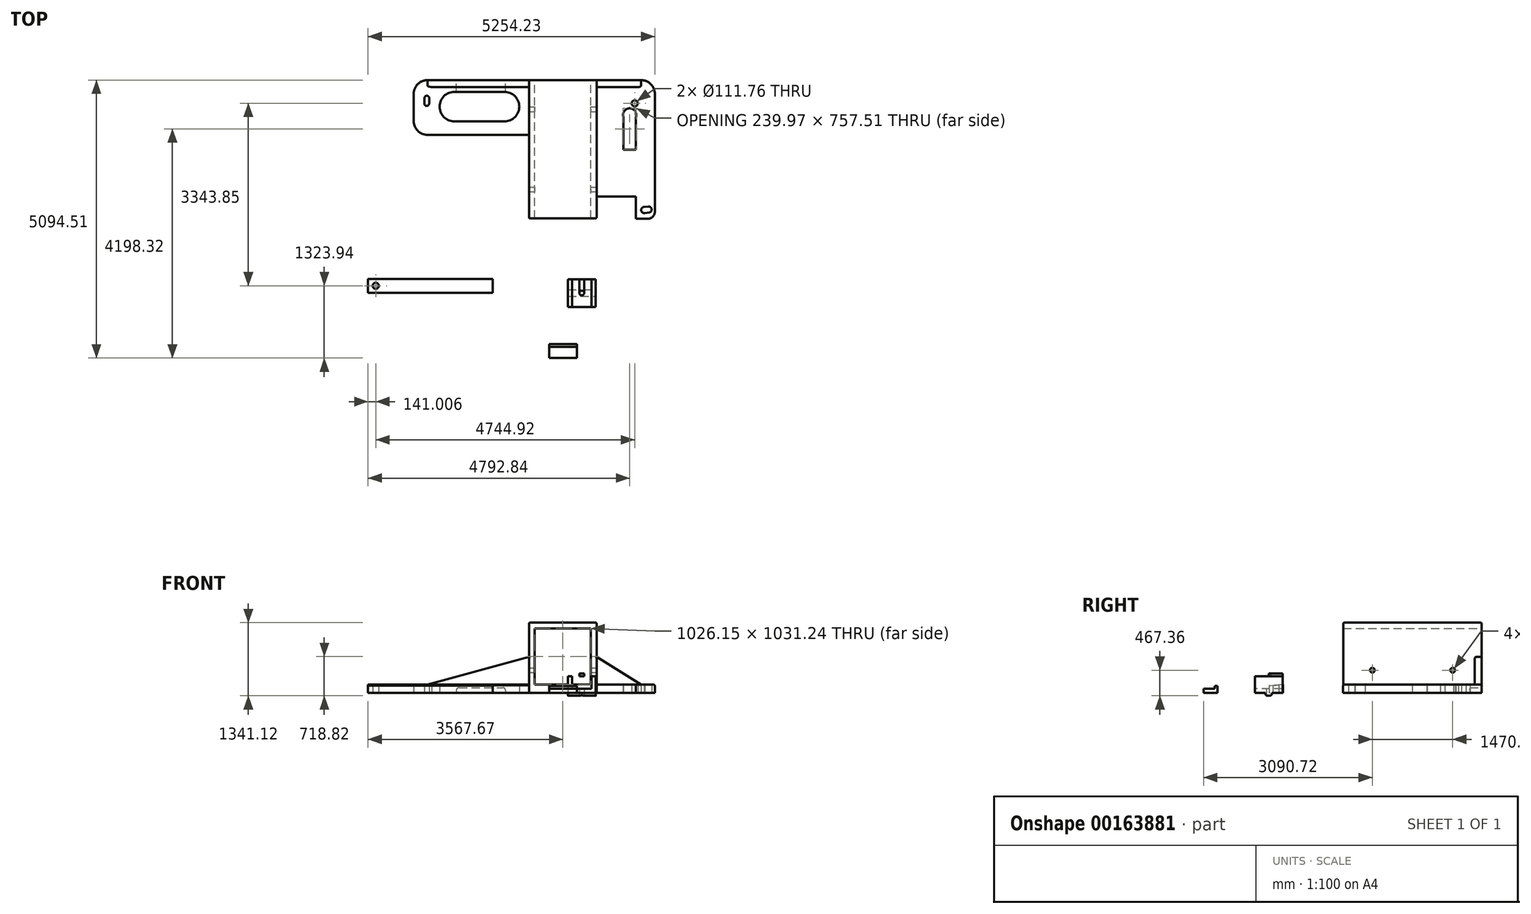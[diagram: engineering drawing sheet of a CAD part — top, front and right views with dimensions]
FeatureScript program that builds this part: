
annotation { "Feature Type Name" : "Feature", "Feature Type Description" : "" }
export const myFeature = defineFeature(function(context is Context, id is Id, definition is map)
    precondition{}
    {
        {
            var Q0;
            Q0=qCreatedBy(makeId("Top.planeOp"),FACE);
            var sketch = newSketch(context, id + "F0", { "sketchPlane" : qUnion([Q0])});
            skLineSegment(sketch, "E0.bottom", {"start": v(-4907.38, 2913.95) * mm, "end": v(2458.62, 2913.95) * mm});
            skLineSegment(sketch, "E0.top", {"start": v(-4907.38, -2928.05) * mm, "end": v(2458.62, -2928.05) * mm});
            skLineSegment(sketch, "E0.left", {"start": v(-4907.38, 2913.95) * mm, "end": v(-4907.38, -2928.05) * mm});
            skLineSegment(sketch, "E0.right", {"start": v(2458.62, 2913.95) * mm, "end": v(2458.62, -2928.05) * mm});
            skCircle(sketch, "E1", {"center": v(-3434.18, 0) * mm, "radius": 55.88 * mm});
            skCircle(sketch, "E2", {"center": v(1823.62, 0) * mm, "radius": 55.88 * mm});
            skCircle(sketch, "E3", {"center": v(1569.62, 1946.9) * mm, "radius": 55.88 * mm});
            skCircle(sketch, "E4", {"center": v(-2240.38, 1943.1) * mm, "radius": 43.18 * mm});
            skLineSegment(sketch, "E5.bottom", {"start": v(-2149.53, 2373.62) * mm, "end": v(1683.92, 2373.62) * mm});
            skLineSegment(sketch, "E5.top", {"start": v(-2149.53, 1372.37) * mm, "end": v(1937.92, 1372.37) * mm});
            skLineSegment(sketch, "E5.left", {"start": v(-2149.53, 2373.62) * mm, "end": v(-2149.53, 1372.37) * mm});
            skLineSegment(sketch, "E5.right", {"start": v(1937.92, 2119.62) * mm, "end": v(1937.92, 1372.37) * mm});
            skLineSegment(sketch, "E6.bottom", {"start": v(1590.86, -167.28) * mm, "end": v(1810.92, -167.28) * mm});
            skLineSegment(sketch, "E6.top", {"start": v(1590.86, 1372.37) * mm, "end": v(1937.92, 1372.37) * mm});
            skLineSegment(sketch, "E6.left", {"start": v(1590.86, -167.28) * mm, "end": v(1590.86, 1372.37) * mm});
            skLineSegment(sketch, "E6.right", {"start": v(1937.92, -40.28) * mm, "end": v(1937.92, 1372.37) * mm});
            skLineSegment(sketch, "E7.bottom", {"start": v(-2354.2, -163.57) * mm, "end": v(-2149.53, -163.57) * mm});
            skLineSegment(sketch, "E7.top", {"start": v(-2227.2, 2373.62) * mm, "end": v(-2149.53, 2373.62) * mm});
            skLineSegment(sketch, "E7.left", {"start": v(-2481.2, -36.57) * mm, "end": v(-2481.2, 2119.62) * mm});
            skLineSegment(sketch, "E7.right", {"start": v(-2149.53, -163.57) * mm, "end": v(-2149.53, 2373.62) * mm});
            skLineSegment(sketch, "E8.bottom", {"start": v(-2149.53, -163.57) * mm, "end": v(1590.86, -163.57) * mm});
            skLineSegment(sketch, "E8.top", {"start": v(-2149.53, 240.98) * mm, "end": v(1590.86, 240.98) * mm});
            skLineSegment(sketch, "E8.right", {"start": v(1590.86, -163.57) * mm, "end": v(1590.86, 240.98) * mm});
            skPoint(sketch, "E9.visualSharp", {"position": v(-2481.2, 2373.62) * mm});
            skArc(sketch, "E9.filletArc", {"start": v(-2227.2, 2373.62) * mm, "mid": v(-2406.8, 2299.22) * mm, "end": v(-2481.2, 2119.62) * mm});
            skPoint(sketch, "E10.visualSharp", {"position": v(1937.92, 2373.62) * mm});
            skArc(sketch, "E10.filletArc", {"start": v(1937.92, 2119.62) * mm, "mid": v(1863.52, 2299.22) * mm, "end": v(1683.92, 2373.62) * mm});
            skPoint(sketch, "E11.visualSharp", {"position": v(-2481.2, -163.57) * mm});
            skArc(sketch, "E11.filletArc", {"start": v(-2481.2, -36.57) * mm, "mid": v(-2444, -126.38) * mm, "end": v(-2354.2, -163.57) * mm});
            skPoint(sketch, "E12.visualSharp", {"position": v(1937.92, -167.28) * mm});
            skArc(sketch, "E12.filletArc", {"start": v(1810.92, -167.28) * mm, "mid": v(1900.72, -130.09) * mm, "end": v(1937.92, -40.28) * mm});
            skLineSegment(sketch, "E13.bottom", {"start": v(-1733.33, 2158.75) * mm, "end": v(-817.71, 2158.75) * mm});
            skLineSegment(sketch, "E13.top", {"start": v(-1733.33, 1615.82) * mm, "end": v(-817.71, 1615.82) * mm});
            skLineSegment(sketch, "E13.left", {"start": v(-1733.33, 2158.75) * mm, "end": v(-1733.33, 1615.82) * mm});
            skLineSegment(sketch, "E13.right", {"start": v(-817.71, 2158.75) * mm, "end": v(-817.71, 1615.82) * mm});
            skArc(sketch, "E14", {"start": v(-817.71, 1615.82) * mm, "mid": v(-546.24, 1887.29) * mm, "end": v(-817.71, 2158.75) * mm});
            skArc(sketch, "E15", {"start": v(-1733.33, 2158.75) * mm, "mid": v(-2004.8, 1887.29) * mm, "end": v(-1733.33, 1615.82) * mm});
            skLineSegment(sketch, "E16", {"start": v(1591.04, 1372.37) * mm, "end": v(1591.04, 1695.24) * mm});
            skLineSegment(sketch, "E17", {"start": v(1591.04, 1695.24) * mm, "end": v(1362.02, 1695.24) * mm});
            skLineSegment(sketch, "E18", {"start": v(1362.02, 1695.24) * mm, "end": v(1362.02, 1372.37) * mm});
            skLineSegment(sketch, "E19", {"start": v(-2481.2, 1370) * mm, "end": v(-2149.53, 1370) * mm});
            skLineSegment(sketch, "E20", {"start": v(-1003, 240.98) * mm, "end": v(-1003, -163.57) * mm});
            skArc(sketch, "E21", {"start": v(1591.04, 1695.24) * mm, "mid": v(1476.53, 1856.18) * mm, "end": v(1362.02, 1695.24) * mm});
            skLineSegment(sketch, "E22", {"start": v(871.12, 2373.62) * mm, "end": v(871.12, -163.57) * mm});
            skLineSegment(sketch, "E23", {"start": v(-368.4, 2373.62) * mm, "end": v(-368.4, -163.57) * mm});
            skPoint(sketch, "E23.endSnap0", {"position": v(-279.34, -163.57) * mm});
            skLineSegment(sketch, "E24", {"start": v(1362.02, 1372.37) * mm, "end": v(1362.02, 1098.67) * mm});
            skLineSegment(sketch, "E25", {"start": v(1362.02, 1098.67) * mm, "end": v(1590.86, 1098.67) * mm});
            skPoint(sketch, "E26", {"position": v(-822.98, 2158.75) * mm});
            skLineSegment(sketch, "E27", {"start": v(-368.4, 2263.35) * mm, "end": v(-2149.53, 2263.35) * mm});
            skLineSegment(sketch, "E28", {"start": v(-368.4, 1472.94) * mm, "end": v(-2149.53, 1472.94) * mm});
            skCircle(sketch, "E29", {"center": v(-2239.2, 2043.15) * mm, "radius": 43.18 * mm});
            skLineSegment(sketch, "E30", {"start": v(-2282.38, 2043.9) * mm, "end": v(-2283.56, 1943.6) * mm});
            skLineSegment(sketch, "E31", {"start": v(-2197.2, 1943.6) * mm, "end": v(-2196.03, 2042.64) * mm});
            skCircle(sketch, "E32", {"center": v(1743.59, -8.78) * mm, "radius": 55.88 * mm});
            skLineSegment(sketch, "E33", {"start": v(1733.46, 46.18) * mm, "end": v(1817.43, 55.54) * mm});
            skLineSegment(sketch, "E34", {"start": v(1745.38, -64.63) * mm, "end": v(1829.6, -55.56) * mm});
            skSolve(sketch);
        }
        {
            var Q0;
            Q0=makeQuery(id+"F0.imprint","IMPRINT",FACE,{"disambiguationData":[TD([[makeQuery(id+"F0.imprint","IMPRINT",EDGE,{"derivedFrom":sQuery(id+"F0.wireOp",EDGE,"E3")}),-1.0]])]});
            var Q1;
            {var subQ0=sQuery(id+"F0.wireOp",EDGE,"E8.right");Q1=makeQuery(id+"F0.imprint","IMPRINT",FACE,{"disambiguationData":[TD([[makeQuery(id+"F0.imprint","IMPRINT",EDGE,{"derivedFrom":subQ0}),1.0]])]});}
            var Q2;
            {var subQ5=sQuery(id+"F0.wireOp",EDGE,"E24");Q2=makeQuery(id+"F0.imprint","IMPRINT",FACE,{"disambiguationData":[TD([[makeQuery(id+"F0.imprint","IMPRINT",EDGE,{"derivedFrom":subQ5}),-1.0]])]});}
            var Q3;
            {var subQ1=sQuery(id+"F0.wireOp",EDGE,"E5.bottom");var subQ4=sQuery(id+"F0.wireOp",EDGE,"E22");var subQ5=makeQuery(id+"F0.imprint","INTERSECT",VERTEX,{"derivedFrom":[subQ1,subQ4]});Q3=makeQuery(id+"F0.imprint","IMPRINT",FACE,{"disambiguationData":[TD([[makeQuery(id+"F0.imprint","IMPRINT",EDGE,{"disambiguationData":[TD([[subQ5,1.0]])],"derivedFrom":subQ1}),-1.0]])]});}
            var Q4;
            {var subQ0=sQuery(id+"F0.wireOp",EDGE,"E23");var subQ1=sQuery(id+"F0.wireOp",EDGE,"E5.top");var subQ2=makeQuery(id+"F0.imprint","INTERSECT",VERTEX,{"derivedFrom":[subQ1,subQ0]});Q4=makeQuery(id+"F0.imprint","IMPRINT",FACE,{"disambiguationData":[TD([[makeQuery(id+"F0.imprint","IMPRINT",EDGE,{"disambiguationData":[TD([[subQ2,-1.0]])],"derivedFrom":subQ1}),-1.0]])]});}
            var Q5;
            {var subQ0=sQuery(id+"F0.wireOp",EDGE,"E22");var subQ1=sQuery(id+"F0.wireOp",EDGE,"E8.bottom");var subQ2=makeQuery(id+"F0.imprint","INTERSECT",VERTEX,{"derivedFrom":[subQ1,subQ0]});Q5=makeQuery(id+"F0.imprint","IMPRINT",FACE,{"disambiguationData":[TD([[makeQuery(id+"F0.imprint","IMPRINT",EDGE,{"disambiguationData":[TD([[subQ2,1.0]])],"derivedFrom":subQ1}),1.0]])]});}
            var Q6;
            Q6=makeQuery(id+"F0.imprint","IMPRINT",FACE,{"disambiguationData":[TD([[makeQuery(id+"F0.imprint","IMPRINT",EDGE,{"derivedFrom":sQuery(id+"F0.wireOp",EDGE,"E13.bottom")}),1.0]])]});
            var Q7;
            {var subQ5=sQuery(id+"F0.wireOp",EDGE,"E28");Q7=makeQuery(id+"F0.imprint","IMPRINT",FACE,{"disambiguationData":[TD([[makeQuery(id+"F0.imprint","IMPRINT",EDGE,{"derivedFrom":subQ5}),1.0]])]});}
            var Q8;
            {var subQ5=sQuery(id+"F0.wireOp",EDGE,"E27");Q8=makeQuery(id+"F0.imprint","IMPRINT",FACE,{"disambiguationData":[TD([[makeQuery(id+"F0.imprint","IMPRINT",EDGE,{"derivedFrom":subQ5}),-1.0]])]});}
            var Q9;
            {var subQ5=sQuery(id+"F0.wireOp",EDGE,"E7.top");Q9=makeQuery(id+"F0.imprint","IMPRINT",FACE,{"disambiguationData":[TD([[makeQuery(id+"F0.imprint","IMPRINT",EDGE,{"derivedFrom":subQ5}),-1.0]])]});}
            var Q10;
            {var subQ10=sQuery(id+"F0.wireOp",EDGE,"E6.bottom");Q10=makeQuery(id+"F0.imprint","IMPRINT",FACE,{"disambiguationData":[TD([[makeQuery(id+"F0.imprint","IMPRINT",EDGE,{"derivedFrom":subQ10}),1.0]])]});}
            extrude(context, id + "F1", {"entities" : qUnion([Q0, Q1, Q2, Q3, Q4, Q5, Q6, Q7, Q8, Q9, Q10]), "depth" : 152.4 * mm});
        }
        {
            var Q0;
            {var subQ1=sQuery(id+"F0.wireOp",EDGE,"E5.bottom");var subQ6=sQuery(id+"F0.wireOp",EDGE,"E22");var subQ8=makeQuery(id+"F0.imprint","INTERSECT",VERTEX,{"derivedFrom":[subQ1,subQ6]});Q0=makeQuery(id+"F0.imprint","IMPRINT",FACE,{"disambiguationData":[TD([[makeQuery(id+"F0.imprint","IMPRINT",EDGE,{"disambiguationData":[TD([[subQ8,1.0]])],"derivedFrom":subQ1}),-1.0]])]});}
            var Q1;
            {var subQ0=sQuery(id+"F0.wireOp",EDGE,"E23");var subQ1=sQuery(id+"F0.wireOp",EDGE,"E5.top");var subQ2=makeQuery(id+"F0.imprint","INTERSECT",VERTEX,{"derivedFrom":[subQ1,subQ0]});Q1=makeQuery(id+"F0.imprint","IMPRINT",FACE,{"disambiguationData":[TD([[makeQuery(id+"F0.imprint","IMPRINT",EDGE,{"disambiguationData":[TD([[subQ2,-1.0]])],"derivedFrom":subQ1}),-1.0]])]});}
            var Q2;
            {var subQ0=sQuery(id+"F0.wireOp",EDGE,"E22");var subQ1=sQuery(id+"F0.wireOp",EDGE,"E8.bottom");var subQ2=makeQuery(id+"F0.imprint","INTERSECT",VERTEX,{"derivedFrom":[subQ1,subQ0]});Q2=makeQuery(id+"F0.imprint","IMPRINT",FACE,{"disambiguationData":[TD([[makeQuery(id+"F0.imprint","IMPRINT",EDGE,{"disambiguationData":[TD([[subQ2,1.0]])],"derivedFrom":subQ1}),1.0]])]});}
            extrude(context, id + "F2", {"entities" : qUnion([Q0, Q1, Q2]), "operationType" : NewBodyOperationType.ADD, "depth" : 1290.32 * mm});
        }
        {
            var Q0;
            {var subQ0=sQuery(id+"F0.wireOp",EDGE,"E5.bottom");Q0=makeQuery(id+"F2.boolean.opBoolean","MERGE",FACE,{"derivedFrom":[makeQuery(id+"F1.opExtrude","SWEPT_FACE",FACE,{"disambiguationData":[OSD([subQ0,sQuery(id+"F0.wireOp",EDGE,"E7.top")])]}),makeQuery(id+"F2.opExtrude","SWEPT_FACE",FACE,{"disambiguationData":[OSD([subQ0])]})]});}
            var sketch = newSketch(context, id + "F3", { "sketchPlane" : qUnion([Q0])});
            skLineSegment(sketch, "E35.bottom", {"start": v(261.71, 152.4) * mm, "end": v(-764.44, 157.48) * mm});
            skLineSegment(sketch, "E35.top", {"start": v(261.71, 1183.64) * mm, "end": v(-764.44, 1183.64) * mm});
            skLineSegment(sketch, "E35.left", {"start": v(261.71, 152.4) * mm, "end": v(261.71, 1183.64) * mm});
            skLineSegment(sketch, "E35.right", {"start": v(-764.44, 157.48) * mm, "end": v(-764.44, 1183.64) * mm});
            skLineSegment(sketch, "E36.bottom", {"start": v(1647.7, 96.52) * mm, "end": v(848.96, 96.52) * mm});
            skLineSegment(sketch, "E36.top", {"start": v(1698.5, 0) * mm, "end": v(798.16, 0) * mm});
            skLineSegment(sketch, "E36.left", {"start": v(1698.5, 45.72) * mm, "end": v(1698.5, 0) * mm});
            skLineSegment(sketch, "E36.right", {"start": v(798.16, 45.72) * mm, "end": v(798.16, 0) * mm});
            skPoint(sketch, "E37.visualSharp", {"position": v(798.16, 96.52) * mm});
            skArc(sketch, "E37.filletArc", {"start": v(848.96, 96.52) * mm, "mid": v(813.04, 81.64) * mm, "end": v(798.16, 45.72) * mm});
            skPoint(sketch, "E38.visualSharp", {"position": v(1698.5, 96.52) * mm});
            skArc(sketch, "E38.filletArc", {"start": v(1698.5, 45.72) * mm, "mid": v(1683.62, 81.64) * mm, "end": v(1647.7, 96.52) * mm});
            skLineSegment(sketch, "E39", {"start": v(368.4, 660.4) * mm, "end": v(2227.2, 152.4) * mm});
            skLineSegment(sketch, "E40", {"start": v(-871.12, 660.4) * mm, "end": v(-1683.92, 152.4) * mm});
            skSolve(sketch);
        }
        {
            var Q0;
            Q0=makeQuery(id+"F3.imprint","IMPRINT",FACE,{"disambiguationData":[TD([[makeQuery(id+"F3.imprint","IMPRINT",EDGE,{"derivedFrom":sQuery(id+"F3.wireOp",EDGE,"E36.bottom")}),1.0]])]});
            extrude(context, id + "F4", {"entities" : qUnion([Q0]), "operationType" : NewBodyOperationType.REMOVE, "oppositeDirection" : true, "depth" : 254 * mm});
        }
        {
            var Q0;
            Q0=makeQuery(id+"F3.imprint","IMPRINT",FACE,{"disambiguationData":[TD([[makeQuery(id+"F3.imprint","IMPRINT",EDGE,{"derivedFrom":sQuery(id+"F3.wireOp",EDGE,"E35.bottom")}),-1.0]])]});
            extrude(context, id + "F5", {"entities" : qUnion([Q0]), "operationType" : NewBodyOperationType.REMOVE, "endBound" : BoundingType.THROUGH_ALL, "oppositeDirection" : true, "depth" : 25.4 * mm});
        }
        {
            var Q0;
            {var subQ0=sQuery(id+"F3.wireOp",EDGE,"E39");Q0=makeQuery(id+"F3.imprint","IMPRINT",FACE,{"disambiguationData":[TD([[makeQuery(id+"F3.imprint","IMPRINT",EDGE,{"derivedFrom":subQ0}),-1.0]])]});}
            var Q1;
            {var subQ0=sQuery(id+"F3.wireOp",EDGE,"E40");Q1=makeQuery(id+"F3.imprint","IMPRINT",FACE,{"disambiguationData":[TD([[makeQuery(id+"F3.imprint","IMPRINT",EDGE,{"derivedFrom":subQ0}),1.0]])]});}
            extrude(context, id + "F6", {"entities" : qUnion([Q0, Q1]), "operationType" : NewBodyOperationType.ADD, "oppositeDirection" : true, "depth" : 127 * mm});
        }
        {
            var Q0;
            Q0=makeQuery(id+"F1.opExtrude","SWEPT_EDGE",EDGE,{"disambiguationData":[OSD([sQuery(id+"F0.wireOp",EDGE,"E7.left"),sQuery(id+"F0.wireOp",EDGE,"E19")])]});
            fillet(context, id + "F7", {"entities" : qUnion([Q0]), "radius" : 254 * mm, "tangentPropagation" : true, "allowEdgeOverflow" : false});
        }
        {
            var Q0;
            Q0=makeQuery(id+"F2.opExtrude","CAP_EDGE",EDGE,{"disambiguationData":[OSD([sQuery(id+"F0.wireOp",EDGE,"E23")])],"isStart":false});
            var Q1;
            Q1=makeQuery(id+"F2.opExtrude","CAP_EDGE",EDGE,{"disambiguationData":[OSD([sQuery(id+"F0.wireOp",EDGE,"E22")])],"isStart":false});
            var Q2;
            Q2=makeQuery(id+"F2.opExtrude","CAP_EDGE",EDGE,{"disambiguationData":[OSD([sQuery(id+"F0.wireOp",EDGE,"E8.bottom")])],"isStart":false});
            var Q3;
            Q3=makeQuery(id+"F2.opExtrude","CAP_EDGE",EDGE,{"disambiguationData":[OSD([sQuery(id+"F0.wireOp",EDGE,"E5.bottom")])],"isStart":false});
            var Q4;
            {var subQ0=sQuery(id+"F0.wireOp",EDGE,"E23");var subQ1=sQuery(id+"F0.wireOp",EDGE,"E8.bottom");Q4=makeQuery(id+"F2.boolean.opBoolean","MERGE",EDGE,{"derivedFrom":[makeQuery(id+"F1.opExtrude","SWEPT_EDGE",EDGE,{"disambiguationData":[OSD([subQ1,subQ0])]}),makeQuery(id+"F2.opExtrude","SWEPT_EDGE",EDGE,{"disambiguationData":[OSD([subQ1,subQ0])]})]});}
            var Q5;
            Q5=makeQuery(id+"F2.opExtrude","SWEPT_EDGE",EDGE,{"disambiguationData":[OSD([sQuery(id+"F0.wireOp",EDGE,"E8.bottom"),sQuery(id+"F0.wireOp",EDGE,"E22")])]});
            var Q6;
            Q6=makeQuery(id+"F2.opExtrude","SWEPT_EDGE",EDGE,{"disambiguationData":[OSD([sQuery(id+"F0.wireOp",EDGE,"E5.bottom"),sQuery(id+"F0.wireOp",EDGE,"E22")])]});
            var Q7;
            Q7=makeQuery(id+"F6.opExtrude","CAP_EDGE",EDGE,{"disambiguationData":[OSD([sQuery(id+"F3.wireOp",EDGE,"E40")])],"isStart":true});
            var Q8;
            Q8=makeQuery(id+"F1.opExtrude","CAP_EDGE",EDGE,{"disambiguationData":[OSD([sQuery(id+"F0.wireOp",EDGE,"E5.right"),sQuery(id+"F0.wireOp",EDGE,"E6.right")])],"isStart":false});
            var Q9;
            Q9=makeQuery(id+"F6.opExtrude","CAP_EDGE",EDGE,{"disambiguationData":[OSD([sQuery(id+"F3.wireOp",EDGE,"E40")])],"isStart":false});
            var Q10;
            Q10=makeQuery(id+"F6.opExtrude","CAP_EDGE",EDGE,{"disambiguationData":[OSD([sQuery(id+"F3.wireOp",EDGE,"E39")])],"isStart":true});
            var Q11;
            Q11=makeQuery(id+"F6.opExtrude","CAP_EDGE",EDGE,{"disambiguationData":[OSD([sQuery(id+"F3.wireOp",EDGE,"E39")])],"isStart":false});
            var Q12;
            Q12=makeQuery(id+"F2.opExtrude","SWEPT_EDGE",EDGE,{"disambiguationData":[OSD([sQuery(id+"F0.wireOp",EDGE,"E5.bottom"),sQuery(id+"F0.wireOp",EDGE,"E23")])]});
            var Q13;
            Q13=makeQuery(id+"F1.opExtrude","CAP_EDGE",EDGE,{"disambiguationData":[OSD([sQuery(id+"F0.wireOp",EDGE,"E7.left")])],"isStart":false});
            fillet(context, id + "F8", {"entities" : qUnion([Q0, Q1, Q2, Q3, Q4, Q5, Q6, Q7, Q8, Q9, Q10, Q11, Q12, Q13]), "radius" : 25.4 * mm, "tangentPropagation" : true, "allowEdgeOverflow" : false});
        }
        {
            var Q0;
            Q0=makeQuery(id+"F2.opExtrude","SWEPT_FACE",FACE,{"disambiguationData":[OSD([sQuery(id+"F0.wireOp",EDGE,"E22")])]});
            var sketch = newSketch(context, id + "F9", { "sketchPlane" : qUnion([Q0])});
            skCircle(sketch, "E41", {"center": v(369.83, 416.56) * mm, "radius": 43.18 * mm});
            skCircle(sketch, "E42", {"center": v(1840.22, 416.56) * mm, "radius": 43.18 * mm});
            skSolve(sketch);
        }
        {
            var Q0;
            Q0 = qSketchRegion(id + "F9", true);
            extrude(context, id + "F10", {"entities" : qUnion([Q0]), "operationType" : NewBodyOperationType.REMOVE, "endBound" : BoundingType.THROUGH_ALL, "oppositeDirection" : true, "depth" : 25.4 * mm});
        }
        {
            var Q0;
            Q0=makeQuery(id+"F0.imprint","IMPRINT",FACE,{"disambiguationData":[TD([[makeQuery(id+"F0.imprint","IMPRINT",EDGE,{"derivedFrom":sQuery(id+"F0.wireOp",EDGE,"E0.bottom")}),-1.0]])]});
            var sketch = newSketch(context, id + "F11", { "sketchPlane" : qUnion([Q0])});
            skLineSegment(sketch, "E43.bottom", {"start": v(-3316.31, -1269.95) * mm, "end": v(-1030.31, -1269.95) * mm});
            skLineSegment(sketch, "E43.top", {"start": v(-3316.31, -1523.95) * mm, "end": v(-1030.31, -1523.95) * mm});
            skLineSegment(sketch, "E43.left", {"start": v(-3316.31, -1269.95) * mm, "end": v(-3316.31, -1523.95) * mm});
            skLineSegment(sketch, "E43.right", {"start": v(-1030.31, -1269.95) * mm, "end": v(-1030.31, -1523.95) * mm});
            skCircle(sketch, "E44", {"center": v(-3175.3, -1396.95) * mm, "radius": 55.88 * mm});
            skPoint(sketch, "E44.centerSnap0", {"position": v(-3316.31, -1396.95) * mm});
            skSolve(sketch);
        }
        {
            var Q0;
            Q0 = qSketchRegion(id + "F11", true);
            extrude(context, id + "F12", {"entities" : qUnion([Q0]), "depth" : 152.4 * mm});
        }
        {
            var Q0;
            Q0=makeQuery(id+"F12.opExtrude","CAP_EDGE",EDGE,{"disambiguationData":[OSD([sQuery(id+"F11.wireOp",EDGE,"E43.top")])],"isStart":false});
            chamfer(context, id + "F13", {"entities" : qUnion([Q0]), "chamferType" : ChamferType.OFFSET_ANGLE, "width" : 254 * mm, "oppositeDirection" : false, "angle" : 4.33 * degree, "tangentPropagation" : true});
        }
        {
            var Q0;
            Q0=makeQuery(id+"F0.imprint","IMPRINT",FACE,{"disambiguationData":[TD([[makeQuery(id+"F0.imprint","IMPRINT",EDGE,{"derivedFrom":sQuery(id+"F0.wireOp",EDGE,"E0.bottom")}),-1.0]])]});
            var sketch = newSketch(context, id + "F14", { "sketchPlane" : qUnion([Q0])});
            skLineSegment(sketch, "E45.bottom", {"start": v(346.21, -1276.41) * mm, "end": v(854.21, -1276.41) * mm});
            skLineSegment(sketch, "E45.top", {"start": v(346.21, -1784.41) * mm, "end": v(854.21, -1784.41) * mm});
            skLineSegment(sketch, "E45.left", {"start": v(346.21, -1276.41) * mm, "end": v(346.21, -1784.41) * mm});
            skLineSegment(sketch, "E45.right", {"start": v(854.21, -1276.41) * mm, "end": v(854.21, -1784.41) * mm});
            skLineSegment(sketch, "E46", {"start": v(600.21, -1276.41) * mm, "end": v(600.21, -1530.41) * mm});
            skPoint(sketch, "E46.endSnap0", {"position": v(854.21, -1530.41) * mm});
            skArc(sketch, "E47.0.startCap", {"start": v(557.03, -1276.41) * mm, "mid": v(600.21, -1233.23) * mm, "end": v(643.4, -1276.41) * mm});
            skArc(sketch, "E47.0.endCap", {"start": v(643.4, -1530.41) * mm, "mid": v(600.21, -1573.6) * mm, "end": v(557.03, -1530.41) * mm});
            skLineSegment(sketch, "E47.0.left", {"start": v(643.4, -1276.41) * mm, "end": v(643.4, -1530.41) * mm});
            skLineSegment(sketch, "E47.0.right", {"start": v(557.03, -1276.41) * mm, "end": v(557.03, -1530.41) * mm});
            skSolve(sketch);
        }
        {
            var Q0;
            Q0=makeQuery(id+"F14.imprint","IMPRINT",FACE,{"disambiguationData":[TD([[makeQuery(id+"F14.imprint","IMPRINT",EDGE,{"derivedFrom":sQuery(id+"F14.wireOp",EDGE,"E45.top")}),1.0]])]});
            extrude(context, id + "F15", {"entities" : qUnion([Q0]), "depth" : 76.2 * mm});
        }
        {
            var Q0;
            Q0=makeQuery(id+"F15.opExtrude","CAP_FACE",FACE,{"disambiguationData":[OSD([sQuery(id+"F14.wireOp",EDGE,"E45.bottom"),sQuery(id+"F14.wireOp",EDGE,"E45.top"),sQuery(id+"F14.wireOp",EDGE,"E45.left"),sQuery(id+"F14.wireOp",EDGE,"E45.right")])],"isStart":false});
            var sketch = newSketch(context, id + "F16", { "sketchPlane" : qUnion([Q0])});
            skLineSegment(sketch, "E48.bottom", {"start": v(346.21, -1276.41) * mm, "end": v(422.41, -1276.41) * mm});
            skLineSegment(sketch, "E48.top", {"start": v(346.21, -1784.41) * mm, "end": v(422.41, -1784.41) * mm});
            skLineSegment(sketch, "E48.left", {"start": v(346.21, -1276.41) * mm, "end": v(346.21, -1784.41) * mm});
            skLineSegment(sketch, "E48.right", {"start": v(422.41, -1276.41) * mm, "end": v(422.41, -1784.41) * mm});
            skLineSegment(sketch, "E49.bottom", {"start": v(854.21, -1276.41) * mm, "end": v(778.01, -1276.41) * mm});
            skLineSegment(sketch, "E49.top", {"start": v(854.21, -1784.41) * mm, "end": v(778.01, -1784.41) * mm});
            skLineSegment(sketch, "E49.left", {"start": v(854.21, -1276.41) * mm, "end": v(854.21, -1784.41) * mm});
            skLineSegment(sketch, "E49.right", {"start": v(778.01, -1276.41) * mm, "end": v(778.01, -1784.41) * mm});
            skPoint(sketch, "E50.centerSnap0", {"position": v(451.62, -1276.41) * mm});
            skPoint(sketch, "E50.centerSnap1", {"position": v(422.41, -1530.41) * mm});
            skSolve(sketch);
        }
        {
            var Q0;
            Q0=makeQuery(id+"F16.imprint","IMPRINT",FACE,{"disambiguationData":[TD([[makeQuery(id+"F16.imprint","IMPRINT",EDGE,{"derivedFrom":sQuery(id+"F16.wireOp",EDGE,"E48.bottom")}),-1.0]])]});
            var Q1;
            Q1=makeQuery(id+"F16.imprint","IMPRINT",FACE,{"disambiguationData":[TD([[makeQuery(id+"F16.imprint","IMPRINT",EDGE,{"derivedFrom":sQuery(id+"F16.wireOp",EDGE,"E49.bottom")}),-1.0]])]});
            extrude(context, id + "F17", {"entities" : qUnion([Q0, Q1]), "operationType" : NewBodyOperationType.ADD, "depth" : 228.6 * mm});
        }
        {
            var Q0;
            Q0=makeQuery(id+"F17.opExtrude","CAP_FACE",FACE,{"disambiguationData":[OSD([sQuery(id+"F16.wireOp",EDGE,"E48.bottom"),sQuery(id+"F16.wireOp",EDGE,"E48.top"),sQuery(id+"F16.wireOp",EDGE,"E48.left"),sQuery(id+"F16.wireOp",EDGE,"E48.right")])],"isStart":false});
            var sketch = newSketch(context, id + "F18", { "sketchPlane" : qUnion([Q0])});
            skLineSegment(sketch, "E51.0.0", {"start": v(422.41, -1784.41) * mm, "end": v(422.41, -1276.41) * mm});
            skLineSegment(sketch, "E51.0.1", {"start": v(422.41, -1276.41) * mm, "end": v(346.21, -1276.41) * mm});
            skLineSegment(sketch, "E51.0.2", {"start": v(346.21, -1276.41) * mm, "end": v(346.21, -1784.41) * mm});
            skLineSegment(sketch, "E51.0.3", {"start": v(346.21, -1784.41) * mm, "end": v(422.41, -1784.41) * mm});
            skLineSegment(sketch, "E52.0.0", {"start": v(557.03, -1276.41) * mm, "end": v(422.41, -1276.41) * mm});
            skLineSegment(sketch, "E52.0.1", {"start": v(422.41, -1276.41) * mm, "end": v(422.41, -1784.41) * mm});
            skLineSegment(sketch, "E52.0.2", {"start": v(422.41, -1784.41) * mm, "end": v(778.01, -1784.41) * mm});
            skLineSegment(sketch, "E52.0.3", {"start": v(778.01, -1784.41) * mm, "end": v(778.01, -1276.41) * mm});
            skLineSegment(sketch, "E52.0.4", {"start": v(778.01, -1276.41) * mm, "end": v(643.4, -1276.41) * mm});
            skLineSegment(sketch, "E52.0.5", {"start": v(643.4, -1276.41) * mm, "end": v(643.4, -1530.41) * mm});
            skArc(sketch, "E52.0.6", {"start": v(643.4, -1530.41) * mm, "mid": v(600.21, -1573.6) * mm, "end": v(557.03, -1530.41) * mm});
            skLineSegment(sketch, "E52.0.7", {"start": v(557.03, -1530.41) * mm, "end": v(557.03, -1276.41) * mm});
            skLineSegment(sketch, "E53.0.0", {"start": v(854.21, -1276.41) * mm, "end": v(778.01, -1276.41) * mm});
            skLineSegment(sketch, "E53.0.1", {"start": v(778.01, -1276.41) * mm, "end": v(778.01, -1784.41) * mm});
            skLineSegment(sketch, "E53.0.2", {"start": v(778.01, -1784.41) * mm, "end": v(854.21, -1784.41) * mm});
            skLineSegment(sketch, "E53.0.3", {"start": v(854.21, -1784.41) * mm, "end": v(854.21, -1276.41) * mm});
            skLineSegment(sketch, "E54.0.0", {"start": v(2458.62, 2913.95) * mm, "end": v(-4907.38, 2913.95) * mm});
            skLineSegment(sketch, "E54.0.1", {"start": v(-4907.38, 2913.95) * mm, "end": v(-4907.38, -2928.05) * mm});
            skLineSegment(sketch, "E54.0.2", {"start": v(-4907.38, -2928.05) * mm, "end": v(2458.62, -2928.05) * mm});
            skLineSegment(sketch, "E54.0.3", {"start": v(2458.62, -2928.05) * mm, "end": v(2458.62, 2913.95) * mm});
            skLineSegment(sketch, "E55.bottom", {"start": v(346.21, -1276.41) * mm, "end": v(854.21, -1276.41) * mm});
            skLineSegment(sketch, "E55.top", {"start": v(346.21, -1784.41) * mm, "end": v(854.21, -1784.41) * mm});
            skLineSegment(sketch, "E55.right", {"start": v(854.21, -1276.41) * mm, "end": v(854.21, -1784.41) * mm});
            skCircle(sketch, "E56", {"center": v(600.21, -1530.41) * mm, "radius": 43.18 * mm});
            skSolve(sketch);
        }
        {
            var Q0;
            {var subQ0=sQuery(id+"F18.wireOp",EDGE,"E52.0.1");Q0=makeQuery(id+"F18.imprint","IMPRINT",FACE,{"disambiguationData":[TD([[makeQuery(id+"F18.imprint","IMPRINT",EDGE,{"derivedFrom":subQ0}),-1.0]])]});}
            var Q1;
            {var subQ3=sQuery(id+"F18.wireOp",EDGE,"E52.0.1");Q1=makeQuery(id+"F18.imprint","IMPRINT",FACE,{"disambiguationData":[TD([[makeQuery(id+"F18.imprint","IMPRINT",EDGE,{"derivedFrom":subQ3}),1.0]])]});}
            var Q2;
            {var subQ0=sQuery(id+"F18.wireOp",EDGE,"E52.0.5");Q2=makeQuery(id+"F18.imprint","IMPRINT",FACE,{"disambiguationData":[TD([[makeQuery(id+"F18.imprint","IMPRINT",EDGE,{"derivedFrom":subQ0}),-1.0]])]});}
            var Q3;
            {var subQ0=sQuery(id+"F18.wireOp",EDGE,"E53.0.1");Q3=makeQuery(id+"F18.imprint","IMPRINT",FACE,{"disambiguationData":[TD([[makeQuery(id+"F18.imprint","IMPRINT",EDGE,{"derivedFrom":subQ0}),1.0]])]});}
            extrude(context, id + "F19", {"entities" : qUnion([Q0, Q1, Q2, Q3]), "operationType" : NewBodyOperationType.ADD, "depth" : 50.8 * mm});
        }
        {
            var Q0;
            Q0=makeQuery(id+"F0.imprint","IMPRINT",FACE,{"disambiguationData":[TD([[makeQuery(id+"F0.imprint","IMPRINT",EDGE,{"derivedFrom":sQuery(id+"F0.wireOp",EDGE,"E0.bottom")}),-1.0]])]});
            var sketch = newSketch(context, id + "F20", { "sketchPlane" : qUnion([Q0])});
            skPoint(sketch, "E57.0", {"position": v(346.21, -1784.41) * mm});
            skPoint(sketch, "E58.0", {"position": v(854.21, -1530.41) * mm});
            skPoint(sketch, "E59.0", {"position": v(346.21, -1530.41) * mm});
            skLineSegment(sketch, "E60.0", {"start": v(346.21, -1784.41) * mm, "end": v(422.41, -1784.41) * mm});
            skLineSegment(sketch, "E61.0.0", {"start": v(2458.62, 2913.95) * mm, "end": v(-4907.38, 2913.95) * mm});
            skLineSegment(sketch, "E61.0.1", {"start": v(-4907.38, 2913.95) * mm, "end": v(-4907.38, -2928.05) * mm});
            skLineSegment(sketch, "E61.0.2", {"start": v(-4907.38, -2928.05) * mm, "end": v(2458.62, -2928.05) * mm});
            skLineSegment(sketch, "E61.0.3", {"start": v(2458.62, -2928.05) * mm, "end": v(2458.62, 2913.95) * mm});
            skLineSegment(sketch, "E62.bottom", {"start": v(346.21, -1591.37) * mm, "end": v(854.21, -1591.37) * mm});
            skLineSegment(sketch, "E62.top", {"start": v(346.21, -1469.45) * mm, "end": v(854.21, -1469.45) * mm});
            skLineSegment(sketch, "E62.left", {"start": v(346.21, -1591.37) * mm, "end": v(346.21, -1469.45) * mm});
            skLineSegment(sketch, "E62.right", {"start": v(854.21, -1591.37) * mm, "end": v(854.21, -1469.45) * mm});
            skLineSegment(sketch, "E63.0", {"start": v(557.03, -1276.41) * mm, "end": v(557.03, -1530.41) * mm});
            skLineSegment(sketch, "E64.0", {"start": v(643.4, -1276.41) * mm, "end": v(643.4, -1530.41) * mm});
            skArc(sketch, "E65.0", {"start": v(643.4, -1530.41) * mm, "mid": v(600.21, -1573.6) * mm, "end": v(557.03, -1530.41) * mm});
            skCircle(sketch, "E66.0", {"center": v(600.21, -1530.41) * mm, "radius": 43.18 * mm});
            skSolve(sketch);
        }
        {
            var Q0;
            Q0=makeQuery(id+"F20.imprint","IMPRINT",FACE,{"disambiguationData":[TD([[makeQuery(id+"F20.imprint","IMPRINT",EDGE,{"derivedFrom":sQuery(id+"F20.wireOp",EDGE,"E62.bottom")}),1.0]])]});
            extrude(context, id + "F21", {"entities" : qUnion([Q0]), "operationType" : NewBodyOperationType.ADD, "oppositeDirection" : true, "depth" : 50.8 * mm});
        }
        {
            var Q0;
            {var subQ0=sQuery(id+"F20.wireOp",EDGE,"E62.top");Q0=makeQuery(id+"F21.opExtrude","CAP_EDGE",EDGE,{"disambiguationData":[OSD([subQ0]),TDD([makeQuery(id+"F20.imprint","IMPRINT",EDGE,{"disambiguationData":[TD([[makeQuery(id+"F20.imprint","INTERSECT",VERTEX,{"derivedFrom":[subQ0,sQuery(id+"F20.wireOp",EDGE,"E62.left")]}),-1.0]])],"derivedFrom":subQ0})])],"isStart":false});}
            var Q1;
            {var subQ0=sQuery(id+"F20.wireOp",EDGE,"E62.top");Q1=makeQuery(id+"F21.opExtrude","CAP_EDGE",EDGE,{"disambiguationData":[OSD([subQ0]),TDD([makeQuery(id+"F20.imprint","IMPRINT",EDGE,{"disambiguationData":[TD([[makeQuery(id+"F20.imprint","INTERSECT",VERTEX,{"derivedFrom":[subQ0,sQuery(id+"F20.wireOp",EDGE,"E62.right")]}),1.0]])],"derivedFrom":subQ0})])],"isStart":false});}
            var Q2;
            Q2=makeQuery(id+"F21.opExtrude","CAP_EDGE",EDGE,{"disambiguationData":[OSD([sQuery(id+"F20.wireOp",EDGE,"E62.bottom")])],"isStart":false});
            fillet(context, id + "F22", {"entities" : qUnion([Q0, Q1, Q2]), "radius" : 38.1 * mm, "tangentPropagation" : true, "allowEdgeOverflow" : false});
        }
        {
            var Q0;
            Q0=qCreatedBy(makeId("Right.planeOp"),FACE);
            var sketch = newSketch(context, id + "F23", { "sketchPlane" : qUnion([Q0])});
            skLineSegment(sketch, "E67", {"start": v(-2466.89, 0) * mm, "end": v(-2720.89, 0) * mm});
            skLineSegment(sketch, "E68", {"start": v(-2720.89, 0) * mm, "end": v(-2720.89, 76.2) * mm});
            skLineSegment(sketch, "E69", {"start": v(-2466.89, 0) * mm, "end": v(-2466.89, 127) * mm});
            skLineSegment(sketch, "E70", {"start": v(-2466.89, 127) * mm, "end": v(-2517.69, 127) * mm});
            skLineSegment(sketch, "E71", {"start": v(-2517.69, 127) * mm, "end": v(-2517.69, 76.2) * mm});
            skLineSegment(sketch, "E72", {"start": v(-2517.69, 76.2) * mm, "end": v(-2720.89, 76.2) * mm});
            skSolve(sketch);
        }
        {
            var Q0;
            Q0=makeQuery(id+"F23.imprint","IMPRINT",FACE,{"disambiguationData":[TD([[makeQuery(id+"F23.imprint","IMPRINT",EDGE,{"derivedFrom":sQuery(id+"F23.wireOp",EDGE,"E67")}),-1.0]])]});
            extrude(context, id + "F24", {"entities" : qUnion([Q0]), "depth" : 508 * mm, "offsetDistance" : 25.4 * mm});
        }
    });
